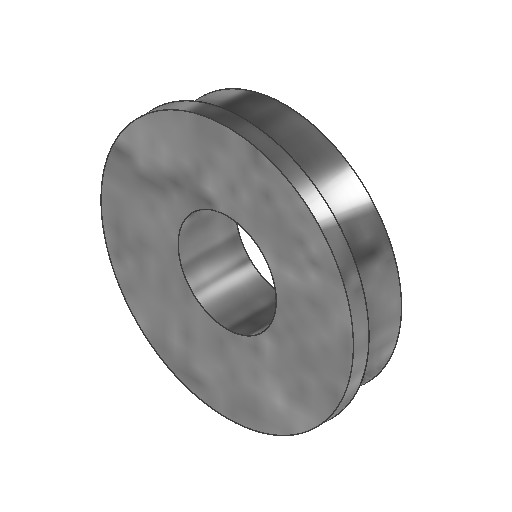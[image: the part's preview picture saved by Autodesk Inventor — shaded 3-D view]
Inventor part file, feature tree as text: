
AUTODESK INVENTOR PART (.ipt)
format: ipt  version: 2025.2 (Build 292293000, 293)  size: 162,816 bytes
history: native  units: in
note: dims shown in document units (in); Inventor stores cm internally (conversion verified against a paired STEP export)
features: extrude x2, sketch x2
ambient origin geometry x8: Origin, YZ Plane, XZ Plane, XY Plane, X Axis, Y Axis, Z Axis, Center Point
bodies: Solid1 (feature_tree)
feature tree (4):
  extrude  "Extrusion1"  Depth=0.315in
  extrude  "Extrusion2"  Depth=0.05in TaperAngle=0.0deg
  sketch  "Sketch1"  dims[d0=0.75in d1=0.315in]
  sketch  "Sketch2"  dims[d2=0.135in d3=0.0in d4=0.05in d5=0.0in]
